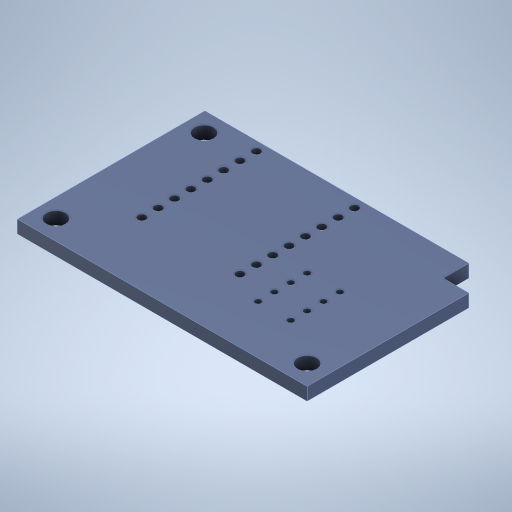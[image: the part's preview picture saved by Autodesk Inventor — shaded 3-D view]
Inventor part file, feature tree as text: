
AUTODESK INVENTOR PART (.ipt)
format: ipt  version: 2024 (Build 280153000, 153)  size: 905,728 bytes
history: native  units: mm
features: other x26, extrude x2, sketch x2, projected_geometry x2
ambient origin geometry x8: Origin, YZ Plane, XZ Plane, XY Plane, X Axis, Y Axis, Z Axis, Center Point
bodies: Volumenkörper1 (feature_tree), Volumenkörper2 (feature_tree), Volumenkörper3 (feature_tree), Volumenkörper4 (feature_tree), Volumenkörper5 (feature_tree), Volumenkörper6 (feature_tree), Volumenkörper7 (feature_tree), Volumenkörper8 (feature_tree), Volumenkörper9 (feature_tree), Volumenkörper10 (feature_tree), Volumenkörper11 (feature_tree), Volumenkörper12 (feature_tree), Volumenkörper13 (feature_tree), Volumenkörper14 (feature_tree), Volumenkörper15 (feature_tree), Volumenkörper16 (feature_tree), Volumenkörper17 (feature_tree), Volumenkörper18 (feature_tree), Volumenkörper19 (feature_tree), Volumenkörper20 (feature_tree), Volumenkörper21 (feature_tree), Volumenkörper22 (feature_tree), Volumenkörper23 (feature_tree), Volumenkörper24 (feature_tree), Volumenkörper25 (feature_tree), Volumenkörper26 (feature_tree)
feature tree (32):
  extrude  "Extrusion1"  Depth=4.0mm
  extrude  "Extrusion2"  Depth=10.0mm TaperAngle=0.0deg
  sketch  "Skizze1"  dims[d0=1.589mm d1=0.0mm d2=4.0mm]
  projected_geometry  "Projizierte Kontur1"
  sketch  "Skizze2"  dims[d3=4.0mm d4=10.0mm d5=0.0mm]
  projected_geometry  "Projizierte Kontur2"
  other  "Open CASCADE STEP translator 7.5 3.1.1_15:1"
  other  "Board c3mini_17:1"
  other  "Board c3mini_17:2"
  other  "Board c3mini_17:3"
  other  "Board c3mini_17:4"
  other  "Board c3mini_17:5"
  other  "Board c3mini_17:6"
  other  "Board c3mini_17:7"
  other  "Board c3mini_17:8"
  other  "Board c3mini_17:9"
  other  "Board c3mini_17:10"
  other  "Board c3mini_17:11"
  other  "Board c3mini_17:12"
  other  "Board c3mini_17:13"
  other  "Board c3mini_17:14"
  other  "Board c3mini_17:15"
  other  "Board c3mini_17:16"
  other  "Board c3mini_17:17"
  other  "USB C_18:1"
  other  "components (other)^ESP32-C3 SuperMini_19:1"
  other  "components (other)^ESP32-C3 SuperMini_19:2"
  other  "components (other)^ESP32-C3 SuperMini_19:3"
  other  "components (other)^ESP32-C3 SuperMini_19:4"
  other  "components (other)^ESP32-C3 SuperMini_19:5"
  other  "components (other)^ESP32-C3 SuperMini_19:6"
  other  "components (other)^ESP32-C3 SuperMini_19:7"
